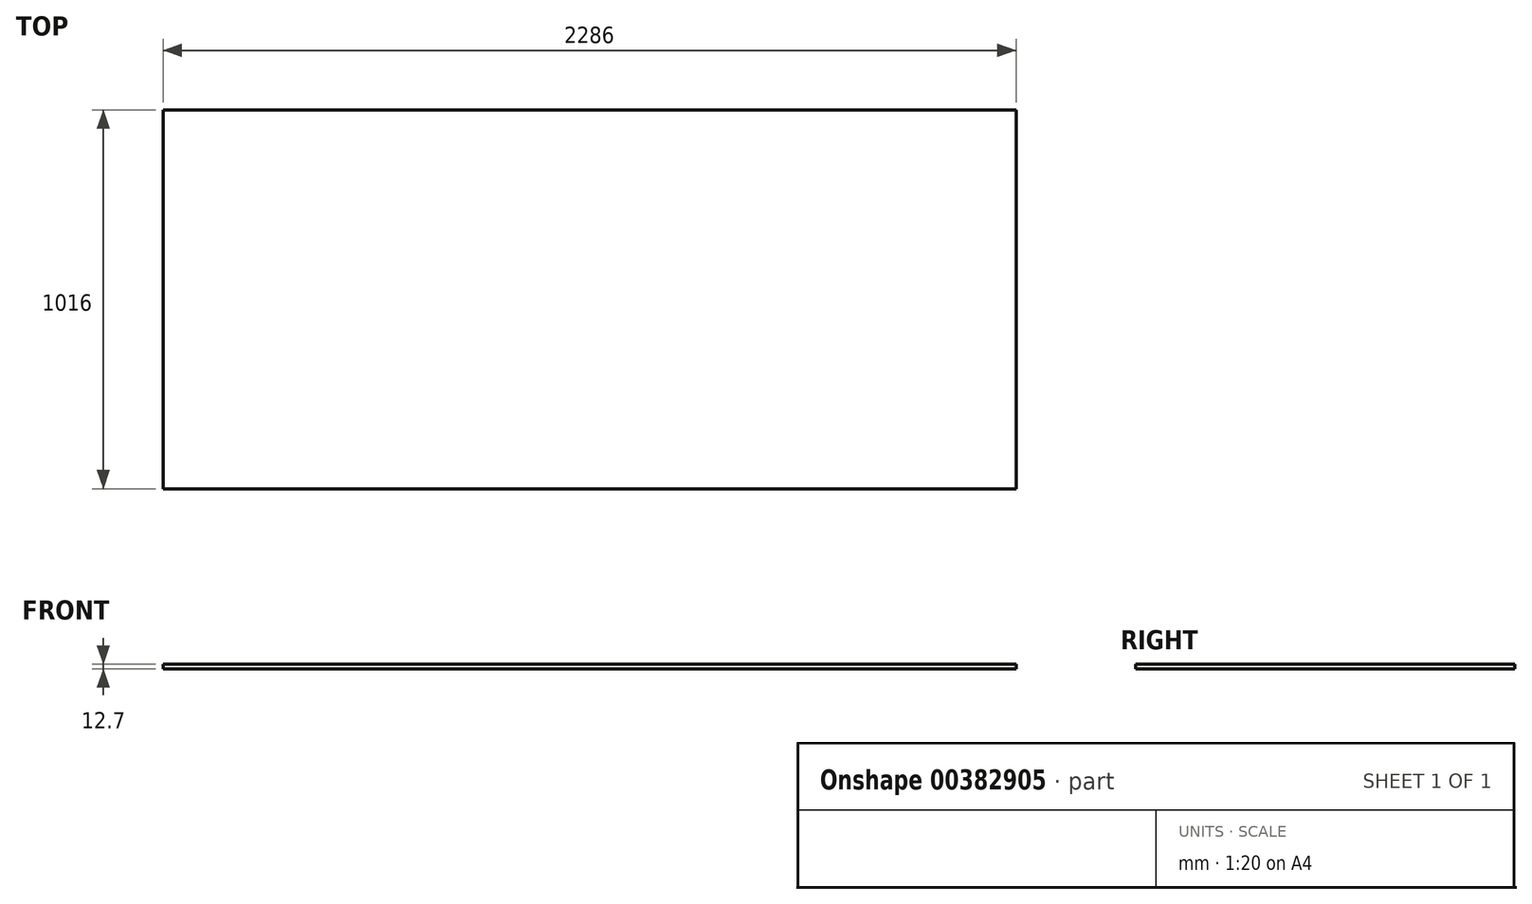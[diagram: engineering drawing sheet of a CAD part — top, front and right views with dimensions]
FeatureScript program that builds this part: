
annotation { "Feature Type Name" : "Feature", "Feature Type Description" : "" }
export const myFeature = defineFeature(function(context is Context, id is Id, definition is map)
    precondition{}
    {
        {
            var Q0;
            Q0=qCreatedBy(makeId("Top.planeOp"),FACE);
            var sketch = newSketch(context, id + "F0", { "sketchPlane" : qUnion([Q0])});
            skLineSegment(sketch, "E0.rect.bottom", {"start": v(1143, 508) * mm, "end": v(-1143, 508) * mm});
            skLineSegment(sketch, "E0.rect.top", {"start": v(1143, -508) * mm, "end": v(-1143, -508) * mm});
            skLineSegment(sketch, "E0.rect.left", {"start": v(1143, 508) * mm, "end": v(1143, -508) * mm});
            skLineSegment(sketch, "E0.rect.right", {"start": v(-1143, 508) * mm, "end": v(-1143, -508) * mm});
            skPoint(sketch, "E0.rect.middle", {"position": v(0, 0) * mm});
            skSolve(sketch);
        }
        {
            var Q0;
            Q0=qSketchRegion(id+"F0",true);
            extrude(context, id + "F1", {"entities" : qUnion([Q0]), "depth" : 12.7 * mm});
        }
    });
